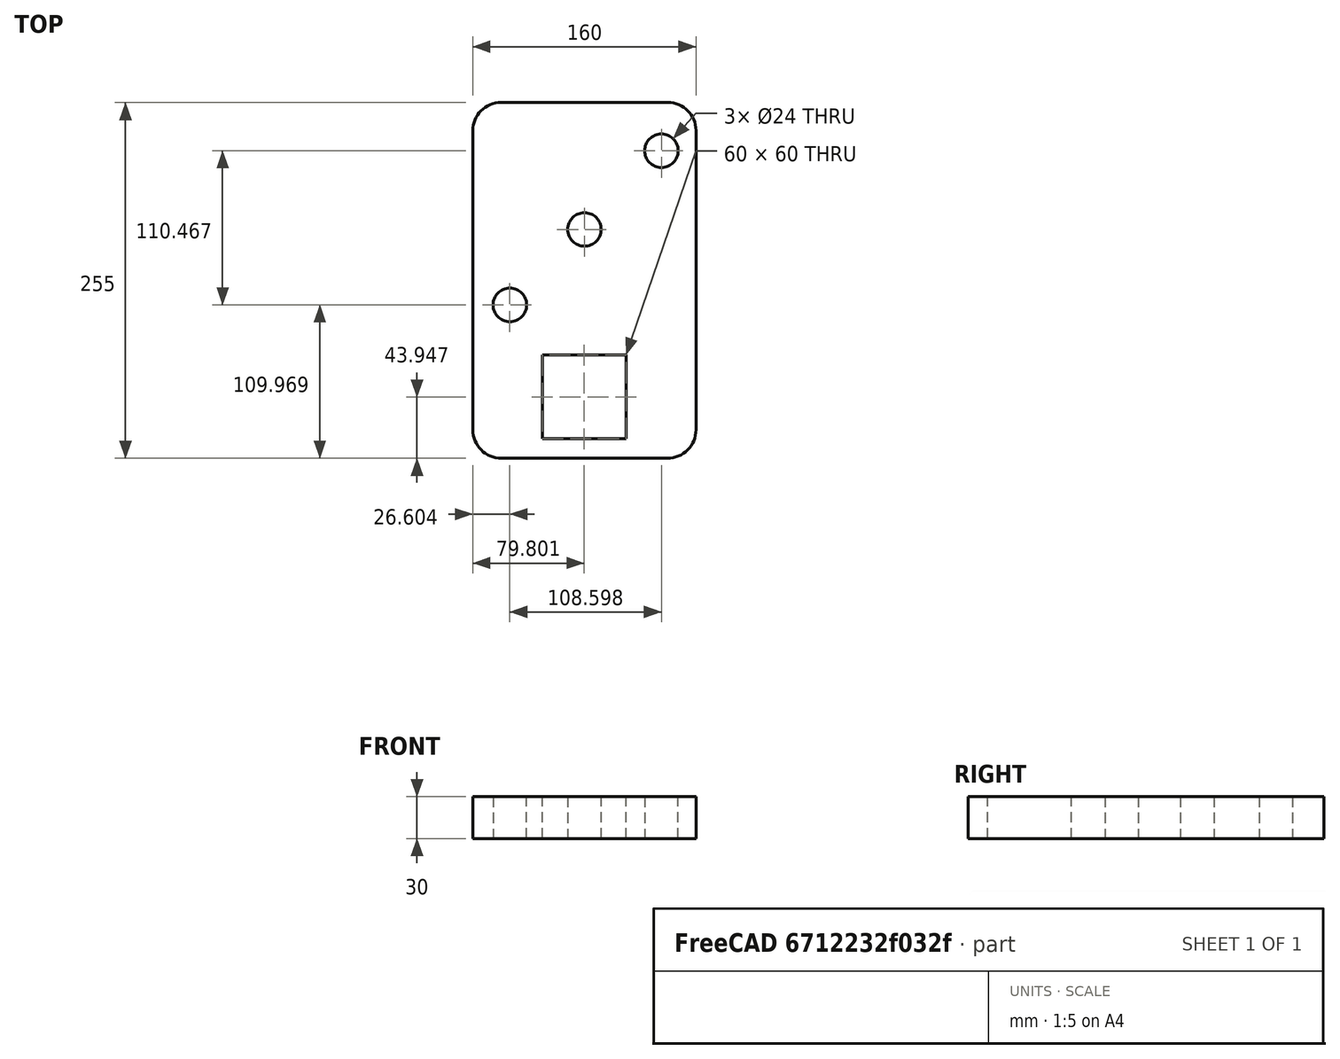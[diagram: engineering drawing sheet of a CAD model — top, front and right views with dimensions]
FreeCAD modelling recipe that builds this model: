
FCSTD DOCUMENT  (FreeCAD 0.18R16131 (Git))
Label: Momentum_Main(2)_Plate_1-1_160X200_12T_12mm(lm12uu)
License: All rights reserved
LicenseURL: http://en.wikipedia.org/wiki/All_rights_reserved
objects: PartDesign::Pad×2, Sketcher::SketchObject×1, PartDesign::Body×1
note: 6 computed .brp shape members not serialized (recipe doc carries the construction recipe); baked Part::Feature solids carry a one-line shape summary decoded from their .brp

FEATURE [Sketcher::SketchObject] Sketch
  MapMode = 5
  Support = -> [XY_Plane]
  sketch-geometry (15):
    g0: Circle CenterX=0.120778 CenterY=29.9192 CenterZ=0 NormalX=0 NormalY=0 NormalZ=1 AngleXU=0 Radius=12
    g1: Circle CenterX=-53.3259 CenterY=-24.1714 CenterZ=0 NormalX=0 NormalY=0 NormalZ=1 AngleXU=0 Radius=12
    g2: Circle CenterX=55.2719 CenterY=86.2952 CenterZ=0 NormalX=0 NormalY=0 NormalZ=1 AngleXU=0 Radius=12
    g3: LineSegment StartX=-30.1291 StartY=-120.193 StartZ=0 EndX=29.8709 EndY=-120.193 EndZ=0
    g4: LineSegment StartX=29.8709 StartY=-120.193 StartZ=0 EndX=29.8709 EndY=-60.1926 EndZ=0
    g5: LineSegment StartX=29.8709 StartY=-60.1926 StartZ=0 EndX=-30.1291 EndY=-60.1926 EndZ=0
    g6: LineSegment StartX=-30.1291 StartY=-60.1926 StartZ=0 EndX=-30.1291 EndY=-120.193 EndZ=0
    g7: LineSegment StartX=-59.3423 StartY=-134.144 StartZ=0 EndX=59.5153 EndY=-134.144 EndZ=0
    g8: LineSegment StartX=80.0668 StartY=-113.592 StartZ=0 EndX=80.0668 EndY=100.872 EndZ=0
    g9: LineSegment StartX=60.0827 StartY=120.856 StartZ=0 EndX=-59.6894 EndY=120.856 EndZ=0
    g10: LineSegment StartX=-79.9332 StartY=100.613 StartZ=0 EndX=-79.9332 EndY=-113.553 EndZ=0
    g11: ArcOfCircle CenterX=60.0827 CenterY=100.872 CenterZ=0 NormalX=0 NormalY=0 NormalZ=1 AngleXU=0 Radius=19.9841 StartAngle=0 EndAngle=1.5708
    g12: ArcOfCircle CenterX=-59.6894 CenterY=100.613 CenterZ=0 NormalX=0 NormalY=0 NormalZ=1 AngleXU=0 Radius=20.2438 StartAngle=1.5708 EndAngle=3.14159
    g13: ArcOfCircle CenterX=59.5153 CenterY=-113.592 CenterZ=0 NormalX=0 NormalY=0 NormalZ=1 AngleXU=0 Radius=20.5515 StartAngle=4.71239 EndAngle=6.28319
    g14: ArcOfCircle CenterX=-59.3423 CenterY=-113.553 CenterZ=0 NormalX=0 NormalY=0 NormalZ=1 AngleXU=0 Radius=20.5909 StartAngle=3.14159 EndAngle=4.71239
  constraints (25):
    c: Radius(g0) = 12
    c: Radius(g1) = 12
    c: Radius(g2) = 12
    c: Coincident(g3,g4)
    c: Coincident(g4,g5)
    c: Coincident(g5,g6)
    c: Coincident(g6,g3)
    c: Horizontal(g3)
    c: Horizontal(g5)
    c: Vertical(g4)
    c: Vertical(g6)
    c: DistanceX(g5,g5) = 60
    c: DistanceY(g4,g4) = 60
    c: Horizontal(g7)
    c: Horizontal(g9)
    c: Vertical(g8)
    c: Vertical(g10)
    c: Tangent(g9,g11) = -1.5708
    c: Tangent(g8,g11) = -1.5708
    c: Tangent(g9,g12) = -1.5708
    c: Tangent(g10,g12) = -1.5708
    c: Tangent(g8,g13) = -1.5708
    c: Tangent(g7,g13) = -1.5708
    c: Tangent(g7,g14) = -1.5708
    c: Tangent(g10,g14) = -1.5708
FEATURE [PartDesign::Pad] Pad
  Length = 30
  Length2 = 100
  Profile = -> Sketch
  Type = 0
FEATURE [PartDesign::Pad] Pad001
  BaseFeature = -> Pad
  Length = 30
  Length2 = 100
  Profile = -> Sketch
  Type = 0
FEATURE [PartDesign::Body] Body
  Group = -> [Sketch,Pad,Pad001]
  Origin = -> Origin
  Tip = -> Pad001
